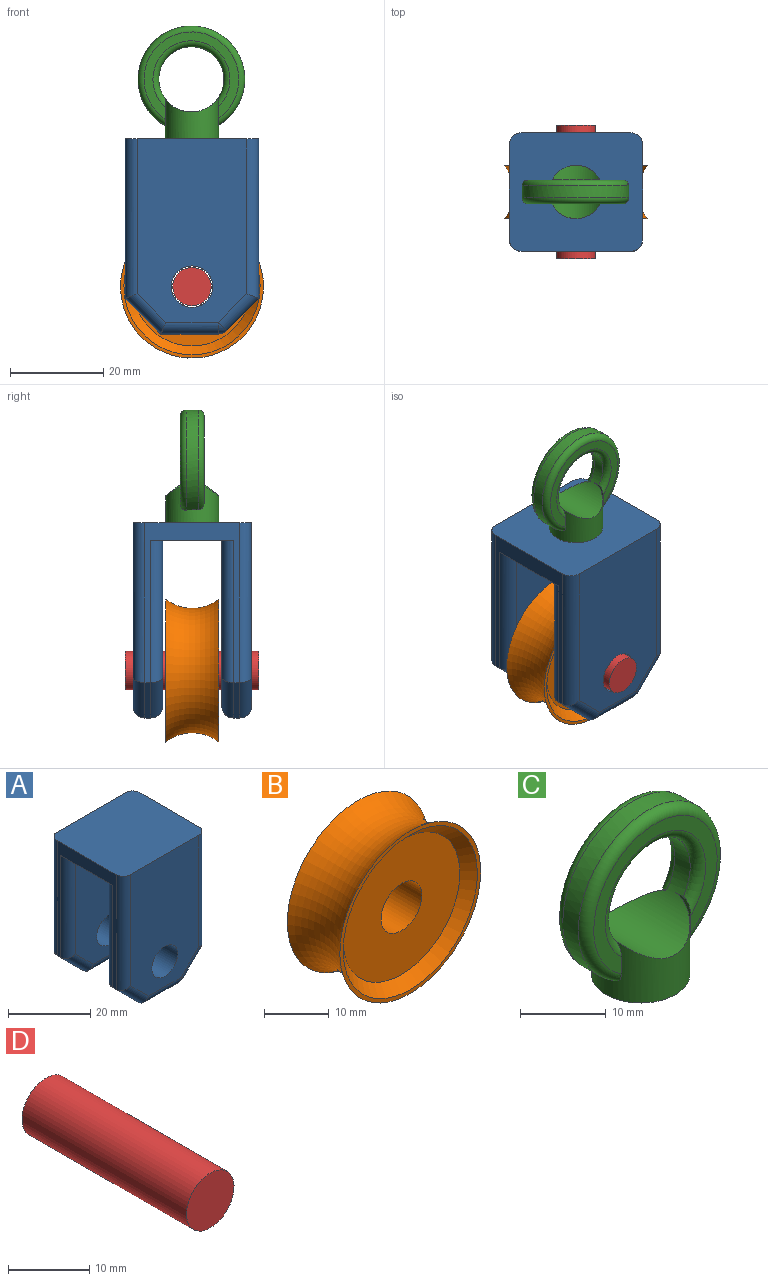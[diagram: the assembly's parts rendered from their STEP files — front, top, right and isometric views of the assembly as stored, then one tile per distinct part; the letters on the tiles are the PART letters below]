
ASSEMBLY  parts=4 mates=3
PART A: 40 faces, bbox 30.4x25.4x41.9 mm
  f0: plane 34.29x20.32mm, normal (1,0,0), area 305.8mm2, adj f5,f6,f7,f9,f10,f11,f25,f26
  f1: plane 34.29x20.32mm, normal (-1,0,0), area 154.8mm2, adj f10,f11,f12,f13,f17,f30,f31,f35
  f2: cylinder r=4.45mm len=8.89mm, axis (0,1,0), area 177.3mm2, adj f4,f5
  f3: plane 12.28x1.27mm, normal (0,0,-1), area 15.6mm2, adj f12,f15,f18,f21
  f4: plane 39.37x23.5mm, normal (0,-1,0), area 825.3mm2, adj f2,f7,f8,f10,f13,f14,f15
  f5: plane 35.56x26.04mm, normal (0,1,0), area 807.3mm2, adj f0,f2,f9,f11,f17,f19,f21
  f6: plane 6.88x6.88mm, normal (0.71,0,-0.71), area 12.3mm2, adj f0,f8,f9,f18
  f7: cylinder r=2.54mm len=34.29mm, axis (0,0,-1), area 135.3mm2, adj f0,f4,f8,f10
  f8: cylinder r=2.54mm len=8.67mm, axis (0.71,0,0.71), area 37.3mm2, adj f4,f6,f7,f16
  f9: cylinder r=2.54mm len=10.47mm, axis (0.71,0,0.71), area 42.5mm2, adj f0,f5,f6,f20
  f10: plane 28.58x25.4mm, normal (0,0,1), area 720.3mm2, adj f0,f1,f4,f7,f13,f24,f27,f31
  f11: plane 28.58x17.78mm, normal (0,0,-1), area 365.7mm2, adj f0,f1,f5,f17,f25,f35
  f12: plane 7.62x7.62mm, normal (-0.71,0,-0.71), area 13.7mm2, adj f1,f3,f14,f19
  f13: cylinder r=2.54mm len=34.29mm, axis (0,0,1), area 135.3mm2, adj f1,f4,f10,f14
  f14: cylinder r=2.54mm len=9.42mm, axis (0.71,0,-0.71), area 39.9mm2, adj f4,f12,f13,f15
  f15: cylinder r=2.54mm len=12.28mm, axis (-1,0,0), area 47.5mm2, adj f3,f4,f14,f16
  f16: sphere r=2.54mm, area 5.1mm2, adj f8,f15,f18
  f17: cylinder r=2.54mm len=30.48mm, axis (0,0,-1), area 120.1mm2, adj f1,f5,f11,f19
  f18: cylinder r=2.54mm len=1.8mm, axis (0,1,0), area 2.5mm2, adj f3,f6,f16,f20
  f19: cylinder r=2.54mm len=9.42mm, axis (0.71,0,-0.71), area 39.9mm2, adj f5,f12,f17,f21
  f20: sphere r=2.54mm, area 5.1mm2, adj f9,f18,f21
  f21: cylinder r=2.54mm len=12.28mm, axis (1,0,0), area 47.5mm2, adj f3,f5,f19,f20
  f22: cylinder r=4.45mm len=8.89mm, axis (0,-1,0), area 177.3mm2, adj f24,f25
  f23: plane 12.28x1.27mm, normal (0,0,-1), area 15.6mm2, adj f30,f33,f36,f39
  f24: plane 39.37x23.5mm, normal (0,1,0), area 825.3mm2, adj f10,f22,f27,f28,f31,f32,f33
  f25: plane 35.56x26.04mm, normal (0,-1,0), area 807.3mm2, adj f0,f11,f22,f29,f35,f37,f39
  f26: plane 6.88x6.88mm, normal (0.71,0,-0.71), area 12.3mm2, adj f0,f28,f29,f36
  f27: cylinder r=2.54mm len=34.29mm, axis (0,0,-1), area 135.3mm2, adj f0,f10,f24,f28
  f28: cylinder r=2.54mm len=8.67mm, axis (0.71,0,0.71), area 37.3mm2, adj f24,f26,f27,f34
  f29: cylinder r=2.54mm len=10.47mm, axis (0.71,0,0.71), area 42.5mm2, adj f0,f25,f26,f38
  f30: plane 7.62x7.62mm, normal (-0.71,0,-0.71), area 13.7mm2, adj f1,f23,f32,f37
  f31: cylinder r=2.54mm len=34.29mm, axis (0,0,1), area 135.3mm2, adj f1,f10,f24,f32
  f32: cylinder r=2.54mm len=9.42mm, axis (0.71,0,-0.71), area 39.9mm2, adj f24,f30,f31,f33
  f33: cylinder r=2.54mm len=12.28mm, axis (-1,0,0), area 47.5mm2, adj f23,f24,f32,f34
  f34: sphere r=2.54mm, area 5.1mm2, adj f28,f33,f36
  f35: cylinder r=2.54mm len=30.48mm, axis (0,0,-1), area 120.1mm2, adj f1,f11,f25,f37
  f36: cylinder r=2.54mm len=1.8mm, axis (0,-1,0), area 2.5mm2, adj f23,f26,f34,f38
  f37: cylinder r=2.54mm len=9.42mm, axis (0.71,0,-0.71), area 39.9mm2, adj f25,f30,f35,f39
  f38: sphere r=2.54mm, area 5.1mm2, adj f29,f36,f39
  f39: cylinder r=2.54mm len=12.28mm, axis (1,0,0), area 47.5mm2, adj f23,f25,f37,f38
PART B: 8 faces, bbox 34.6x13.1x34.6 mm
  f0: plane 30.65x30.65mm, normal (0,-1,0), area 67.5mm2, adj f6,f7
  f1: plane 30.65x30.65mm, normal (0,1,0), area 67.5mm2, adj f5,f7
  f2: cylinder r=4.45mm len=8.89mm, axis (0,1,0), area 212.8mm2, adj f3,f4
  f3: plane 25.4x25.4mm, normal (0,-1,0), area 444.6mm2, adj f2,f6
  f4: plane 25.4x25.4mm, normal (0,1,0), area 444.6mm2, adj f2,f5
  f5: cone r=14.61mm half-angle=45deg, axis (0,1,0), area 231.1mm2, adj f1,f4
  f6: cone r=12.7mm half-angle=45deg, axis (0,-1,0), area 231.1mm2, adj f0,f3
  f7: torus R=22.54mm, axis (0,1,0), area 1085.3mm2, adj f0,f1
PART C: 13 faces, bbox 20000000000000000038313501714693374724319102545303840223056070291987586484079775119224722902163606470656x20000000000000000038313501714693374724319102545303840223056070291987586484079775119224722902163606470656x20000000000000000038313501714693374724319102545303840223056070291987586484079775119224722902163606470656 mm
  f0: cylinder r=5.71mm len=11.43mm, axis (0,0,-1), area 226.7mm2, adj f1,f2,f3,f4,f8,f9,f10,f11
  f1: torus R=8.26mm, axis (0,1,0), area 69.7mm2, adj f0,f2,f9
  f2: plane 20.32x19.01mm, normal (0,1,0), area 89.5mm2, adj f0,f1,f3
  f3: torus R=10.16mm, axis (0,1,0), area 115.4mm2, adj f0,f2,f4
  f4: cylinder r=11.43mm len=22.86mm, axis (0,-1,0), area 152.2mm2, adj f0,f3,f5,f8,f10
  f5: torus R=10.16mm, axis (0,1,0), area 113.5mm2, adj f4,f6,f8,f10
  f6: plane 20.32x18.65mm, normal (0,-1,0), area 86.7mm2, adj f5,f7,f8,f10
  f7: torus R=8.26mm, axis (0,1,0), area 67.3mm2, adj f6,f8,f9,f10
  f8: plane 5.78x2.54mm, normal (1,0,0), area 13.7mm2, adj f0,f4,f5,f6,f7,f9
  f9: cylinder r=6.99mm len=13.97mm, axis (0,-1,0), area 192.4mm2, adj f0,f1,f7,f8,f10
  f10: plane 6x2.54mm, normal (-1,0,0), area 14.2mm2, adj f0,f4,f5,f6,f7,f9
  f11: plane 11.43x11.43mm, normal (0,0,-1), area 102.6mm2, adj f0
  f12: cylinder r=6.99mm len=20000000000000000038313501714693374724319102545303840223056070291987586484079775119224722902163606470656mm, axis (0,-1,0), area 558799999999999954600596027778069046798558458276849996845563873453962448728234915934315357035332554981376mm2
PART D: 3 faces, bbox 8.3x28.6x8.3 mm
  f0: cylinder r=4.13mm len=28.58mm, axis (0,1,0), area 741.1mm2, adj f1,f2
  f1: plane 8.26x8.26mm, normal (0,-1,0), area 53.5mm2, adj f0
  f2: plane 8.26x8.26mm, normal (0,1,0), area 53.5mm2, adj f0
PLACE A t=(0.29,-29.01,-3.51)mm
PLACE B t=(-14,-22.66,1.57)mm fixed
PLACE C t=(0.29,-29.01,-3.51)mm
PLACE D t=(-14,-8.31,1.57)mm
MATE cylindrical B.f7 <-> D.f0  axis (0,1,0) through (-14,-22.66,1.57)mm
MATE fastened A.f10 <-> C.f0  axis (0,0,1) through (-14,-22.66,33.32)mm
MATE slider A.f2 <-> D.f0  axis (0,-1,0) through (-14,-9.96,1.57)mm
